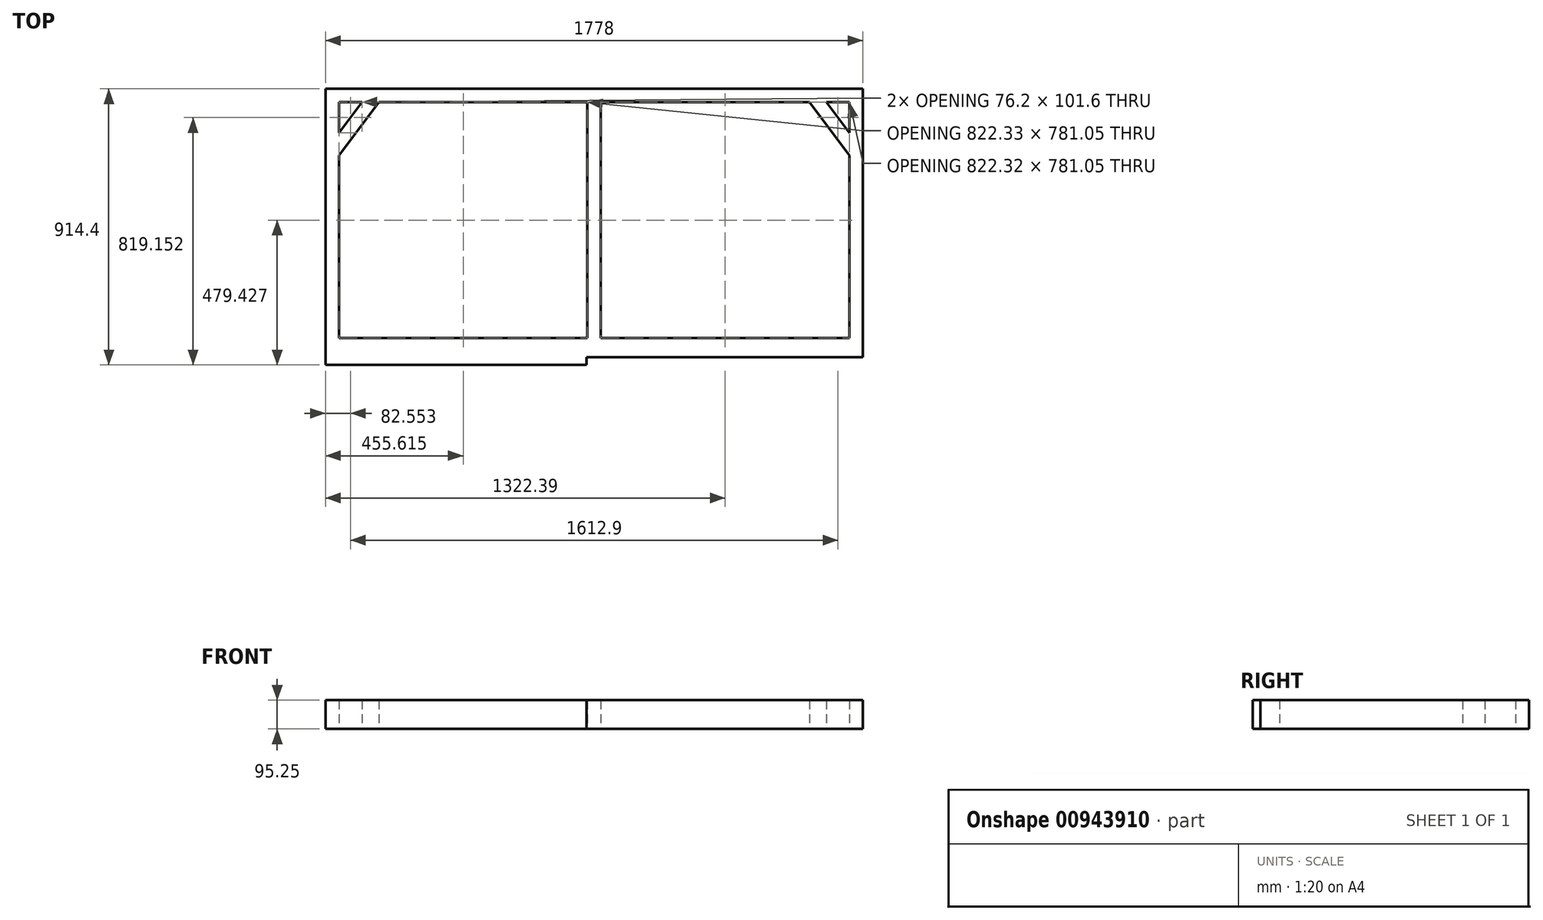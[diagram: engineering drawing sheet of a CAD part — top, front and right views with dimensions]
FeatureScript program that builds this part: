
annotation { "Feature Type Name" : "Feature", "Feature Type Description" : "" }
export const myFeature = defineFeature(function(context is Context, id is Id, definition is map)
    precondition{}
    {
        {
            var Q0;
            Q0=qCreatedBy(makeId("Top.planeOp"),FACE);
            var sketch = newSketch(context, id + "F0", { "sketchPlane" : qUnion([Q0])});
            skLineSegment(sketch, "E0.bottom", {"start": v(-895.07, 558.91) * mm, "end": v(882.93, 558.91) * mm});
            skLineSegment(sketch, "E0.top", {"start": v(-895.07, -355.49) * mm, "end": v(-31.47, -355.49) * mm});
            skLineSegment(sketch, "E0.left", {"start": v(-895.07, 558.91) * mm, "end": v(-895.07, -355.49) * mm});
            skLineSegment(sketch, "E0.right", {"start": v(882.93, 558.91) * mm, "end": v(882.93, -330.09) * mm});
            skLineSegment(sketch, "E1.top", {"start": v(882.93, -330.09) * mm, "end": v(-31.47, -330.09) * mm});
            skLineSegment(sketch, "E1.right", {"start": v(-31.47, -355.49) * mm, "end": v(-31.47, -330.09) * mm});
            skPoint(sketch, "E2.orphan", {"position": v(882.93, -355.49) * mm});
            skLineSegment(sketch, "E3.0", {"start": v(-850.62, 514.46) * mm, "end": v(-850.62, -266.59) * mm});
            skLineSegment(sketch, "E3.1", {"start": v(838.48, 514.46) * mm, "end": v(838.48, -266.59) * mm});
            skLineSegment(sketch, "E3.3", {"start": v(-850.62, 514.46) * mm, "end": v(838.48, 514.46) * mm});
            skLineSegment(sketch, "E4", {"start": v(-850.62, 514.46) * mm, "end": v(-895.07, 514.46) * mm});
            skLineSegment(sketch, "E5", {"start": v(838.48, 514.46) * mm, "end": v(882.93, 514.46) * mm});
            skLineSegment(sketch, "E6", {"start": v(-850.62, -266.59) * mm, "end": v(838.48, -266.59) * mm});
            skLineSegment(sketch, "E7", {"start": v(-895.07, -311.04) * mm, "end": v(882.93, -311.04) * mm});
            skLineSegment(sketch, "E8", {"start": v(-850.62, -266.59) * mm, "end": v(-850.62, -311.04) * mm});
            skLineSegment(sketch, "E9", {"start": v(838.48, -266.59) * mm, "end": v(838.48, -311.04) * mm});
            skPoint(sketch, "E10.orphan", {"position": v(-895.07, -266.59) * mm});
            skLineSegment(sketch, "E11.0", {"start": v(-28.3, 514.46) * mm, "end": v(-28.3, -266.59) * mm});
            skLineSegment(sketch, "E12.0", {"start": v(16.16, 514.46) * mm, "end": v(16.16, -266.59) * mm});
            skPoint(sketch, "E13.start.orphan", {"position": v(-6.07, 514.46) * mm});
            skLineSegment(sketch, "E14", {"start": v(-774.42, 514.46) * mm, "end": v(-850.62, 412.86) * mm});
            skLineSegment(sketch, "E15", {"start": v(-718.85, 514.46) * mm, "end": v(-850.62, 338.78) * mm});
            skLineSegment(sketch, "E16", {"start": v(762.28, 514.46) * mm, "end": v(838.48, 412.86) * mm});
            skLineSegment(sketch, "E17", {"start": v(706.72, 514.46) * mm, "end": v(838.48, 338.78) * mm});
            skSolve(sketch);
        }
        {
            var Q0;
            {var subQ8=sQuery(id+"F0.wireOp",EDGE,"E0.bottom");Q0=makeQuery(id+"F0.imprint","IMPRINT",FACE,{"disambiguationData":[TD([[makeQuery(id+"F0.imprint","IMPRINT",EDGE,{"derivedFrom":subQ8}),-1.0]])]});}
            var Q1;
            {var subQ3=sQuery(id+"F0.wireOp",EDGE,"E4");Q1=makeQuery(id+"F0.imprint","IMPRINT",FACE,{"disambiguationData":[TD([[makeQuery(id+"F0.imprint","IMPRINT",EDGE,{"derivedFrom":subQ3}),1.0]])]});}
            var Q2;
            {var subQ0=sQuery(id+"F0.wireOp",EDGE,"E14");Q2=makeQuery(id+"F0.imprint","IMPRINT",FACE,{"disambiguationData":[TD([[makeQuery(id+"F0.imprint","IMPRINT",EDGE,{"derivedFrom":subQ0}),1.0]])]});}
            var Q3;
            {var subQ0=sQuery(id+"F0.wireOp",EDGE,"E11.0");Q3=makeQuery(id+"F0.imprint","IMPRINT",FACE,{"disambiguationData":[TD([[makeQuery(id+"F0.imprint","IMPRINT",EDGE,{"derivedFrom":subQ0}),1.0]])]});}
            var Q4;
            {var subQ0=sQuery(id+"F0.wireOp",EDGE,"E16");Q4=makeQuery(id+"F0.imprint","IMPRINT",FACE,{"disambiguationData":[TD([[makeQuery(id+"F0.imprint","IMPRINT",EDGE,{"derivedFrom":subQ0}),-1.0]])]});}
            var Q5;
            {var subQ4=sQuery(id+"F0.wireOp",EDGE,"E5");Q5=makeQuery(id+"F0.imprint","IMPRINT",FACE,{"disambiguationData":[TD([[makeQuery(id+"F0.imprint","IMPRINT",EDGE,{"derivedFrom":subQ4}),-1.0]])]});}
            var Q6;
            {var subQ0=sQuery(id+"F0.wireOp",EDGE,"E8");Q6=makeQuery(id+"F0.imprint","IMPRINT",FACE,{"disambiguationData":[TD([[makeQuery(id+"F0.imprint","IMPRINT",EDGE,{"derivedFrom":subQ0}),1.0]])]});}
            var Q7;
            {var subQ7=sQuery(id+"F0.wireOp",EDGE,"E0.top");Q7=makeQuery(id+"F0.imprint","IMPRINT",FACE,{"disambiguationData":[TD([[makeQuery(id+"F0.imprint","IMPRINT",EDGE,{"derivedFrom":subQ7}),1.0]])]});}
            extrude(context, id + "F1", {"entities" : qUnion([Q0, Q1, Q2, Q3, Q4, Q5, Q6, Q7]), "depth" : 95.25 * mm, "offsetDistance" : 25.4 * mm});
        }
    });
